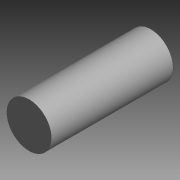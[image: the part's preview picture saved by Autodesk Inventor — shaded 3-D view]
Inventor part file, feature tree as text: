
AUTODESK INVENTOR PART (.ipt)
format: ipt  version: 2014 SP1 (Build 180222100, 222)  size: 68,608 bytes
history: native  units: in
note: dims shown in document units (in); Inventor stores cm internally (conversion verified against a paired STEP export)
features: extrude x1, sketch x1
ambient origin geometry x8: Origin, YZ Plane, XZ Plane, XY Plane, X Axis, Y Axis, Z Axis, Center Point
bodies: Solid1 (feature_tree)
feature tree (2):
  extrude  "Extrusion1"  Depth=0.5906in TaperAngle=0.0deg
  sketch  "Sketch1"  dims[d0=0.1437in d1=0.5906in d2=0.0in]
